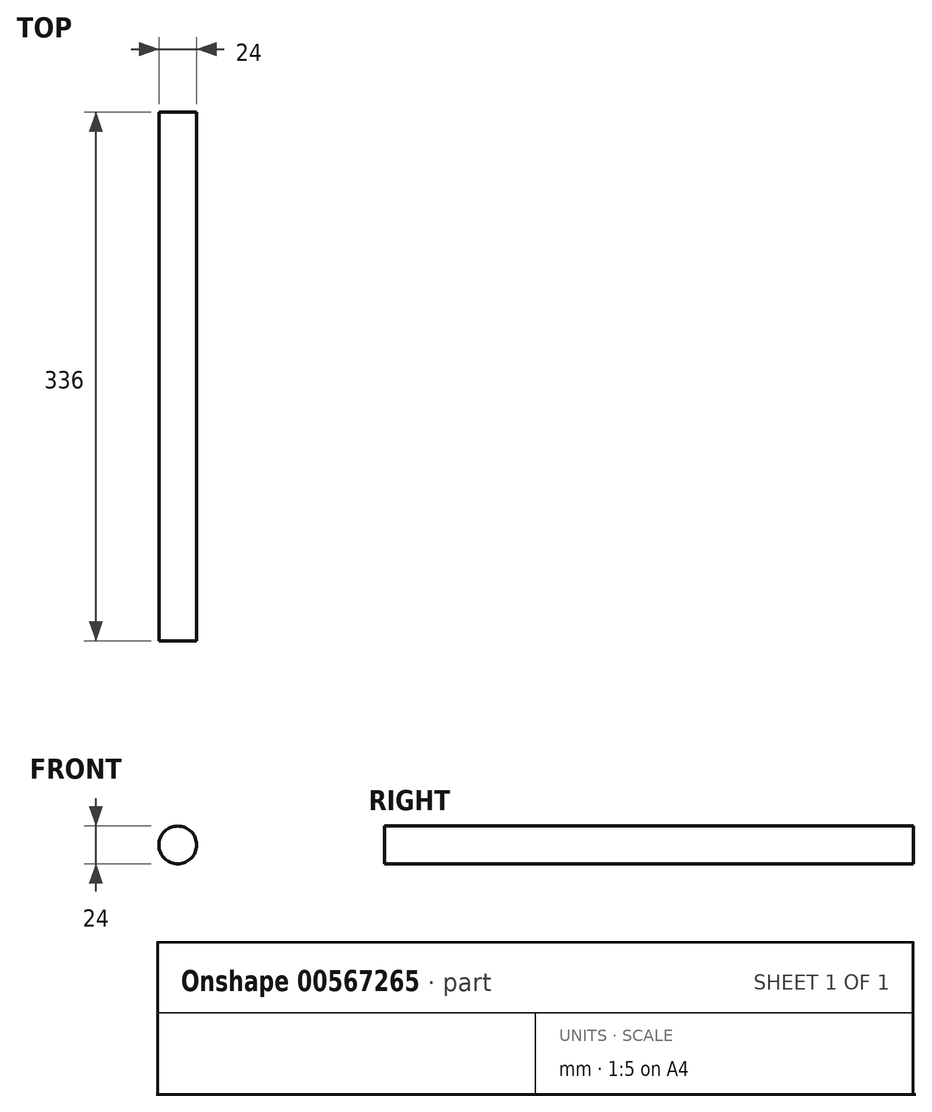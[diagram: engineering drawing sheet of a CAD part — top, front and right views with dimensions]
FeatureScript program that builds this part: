
annotation { "Feature Type Name" : "Feature", "Feature Type Description" : "" }
export const myFeature = defineFeature(function(context is Context, id is Id, definition is map)
    precondition{}
    {
        {
            var Q0;
            Q0=qCreatedBy(makeId("Front.planeOp"),FACE);
            var sketch = newSketch(context, id + "F0", { "sketchPlane" : qUnion([Q0])});
            skCircle(sketch, "E0", {"center": v(-25.64, 13.68) * mm, "radius": 12 * mm});
            skSolve(sketch);
        }
        {
            var Q0;
            Q0=makeQuery(id+"F0.imprint","IMPRINT",FACE,{"disambiguationData":[TD([[makeQuery(id+"F0.imprint","IMPRINT",EDGE,{"derivedFrom":sQuery(id+"F0.wireOp",EDGE,"E0")}),1.0]])]});
            extrude(context, id + "F1", {"entities" : qUnion([Q0]), "depth" : 336 * mm, "offsetDistance" : 25 * mm});
        }
    });
